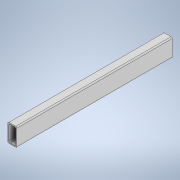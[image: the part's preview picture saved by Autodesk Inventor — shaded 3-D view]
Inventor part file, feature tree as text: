
AUTODESK INVENTOR PART (.ipt)
format: ipt  version: 2020 (Build 240168000, 168)  size: 119,808 bytes
history: native  units: in
note: dims shown in document units (in); Inventor stores cm internally (conversion verified against a paired STEP export)
features: extrude x1, sketch x1
ambient origin geometry x8: Origin, YZ Plane, XZ Plane, XY Plane, X Axis, Y Axis, Z Axis, Center Point
bodies: Solid1 (feature_tree)
feature tree (2):
  extrude  "Extrusion1"  Depth=1.0in
  sketch  "Sketch1"  dims[d0=2.0in d1=1.0in d2=0.125in d3=0.125in d4=0.125in d5=0.125in d6=0.125in d7=0.125in d8=0.125in d9=0.125in d10=0.125in d11=17.0in d12=0.0in]
